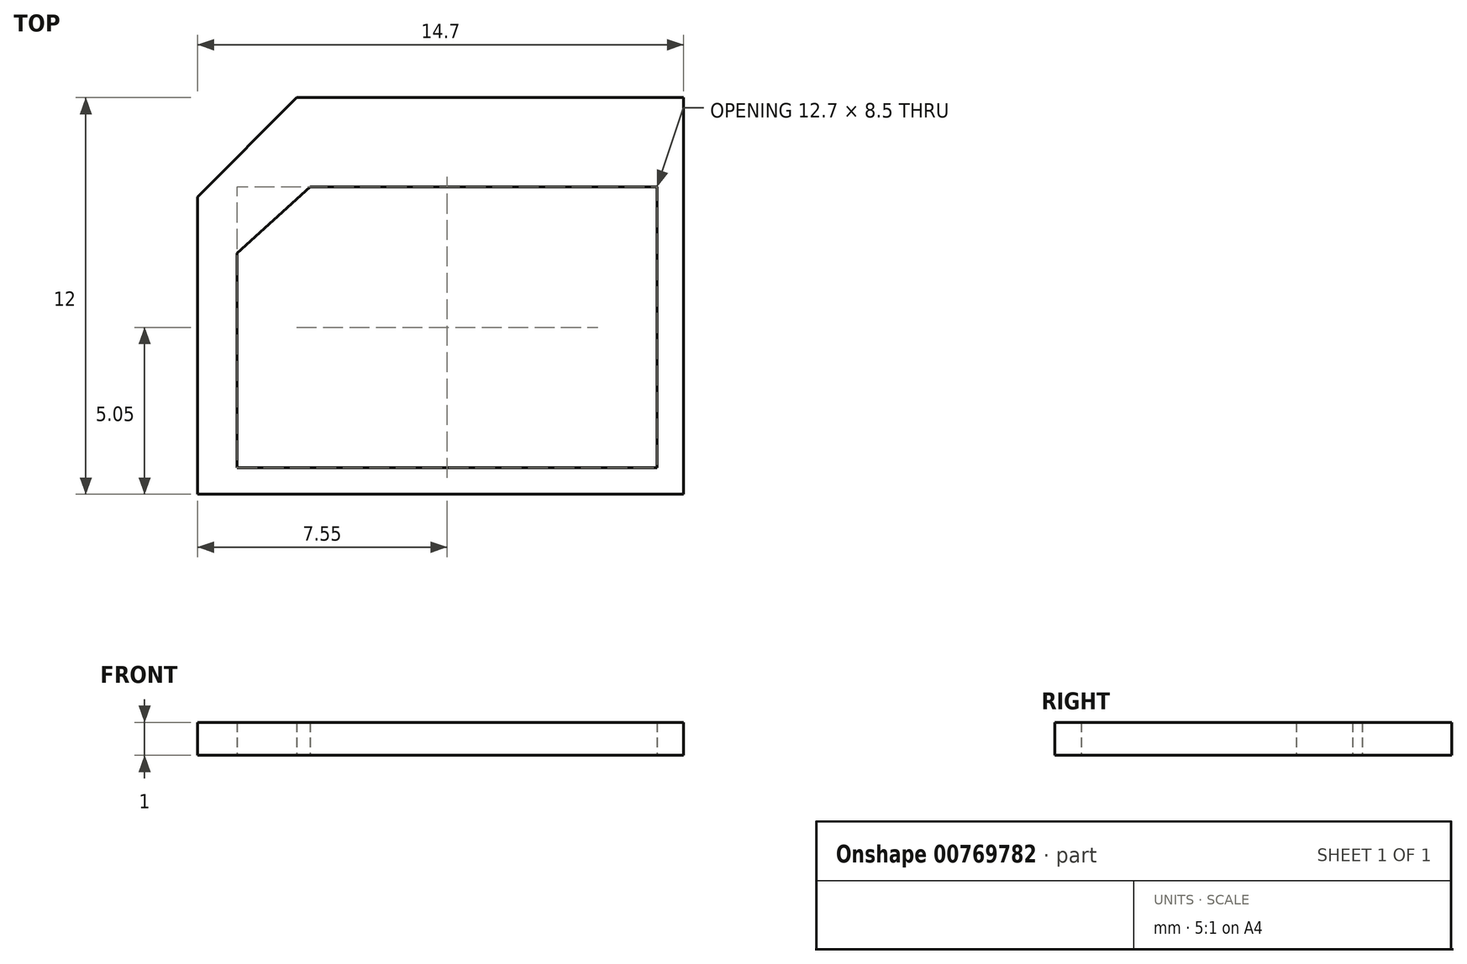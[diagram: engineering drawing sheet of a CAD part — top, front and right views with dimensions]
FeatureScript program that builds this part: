
annotation { "Feature Type Name" : "Feature", "Feature Type Description" : "" }
export const myFeature = defineFeature(function(context is Context, id is Id, definition is map)
    precondition{}
    {
        {
            var Q0;
            Q0=qCreatedBy(makeId("Top.planeOp"),FACE);
            var sketch = newSketch(context, id + "F0", { "sketchPlane" : qUnion([Q0])});
            skLineSegment(sketch, "E0", {"start": v(-12.7, 0) * mm, "end": v(0, 0) * mm});
            skLineSegment(sketch, "E1", {"start": v(0, 0) * mm, "end": v(0, 8.5) * mm});
            skLineSegment(sketch, "E2", {"start": v(-12.7, 0) * mm, "end": v(-12.7, 6.5) * mm});
            skLineSegment(sketch, "E3", {"start": v(0, 8.5) * mm, "end": v(-10.5, 8.5) * mm});
            skLineSegment(sketch, "E4", {"start": v(-10.5, 8.5) * mm, "end": v(-12.7, 6.5) * mm});
            skLineSegment(sketch, "E5", {"start": v(0.8, -0.8) * mm, "end": v(-13.9, -0.8) * mm});
            skLineSegment(sketch, "E6", {"start": v(0.8, -0.8) * mm, "end": v(0.8, 11.2) * mm});
            skLineSegment(sketch, "E7", {"start": v(0.8, 11.2) * mm, "end": v(-10.9, 11.2) * mm});
            skLineSegment(sketch, "E8", {"start": v(-13.9, -0.8) * mm, "end": v(-13.9, 8.2) * mm});
            skLineSegment(sketch, "E9", {"start": v(-10.9, 11.2) * mm, "end": v(-13.9, 8.2) * mm});
            skSolve(sketch);
        }
        {
            var Q0;
            Q0 = qSketchRegion(id + "F0", true);
            extrude(context, id + "F1", {"entities" : qUnion([Q0]), "depth" : 1 * mm, "offsetDistance" : 25 * mm});
        }
    });
